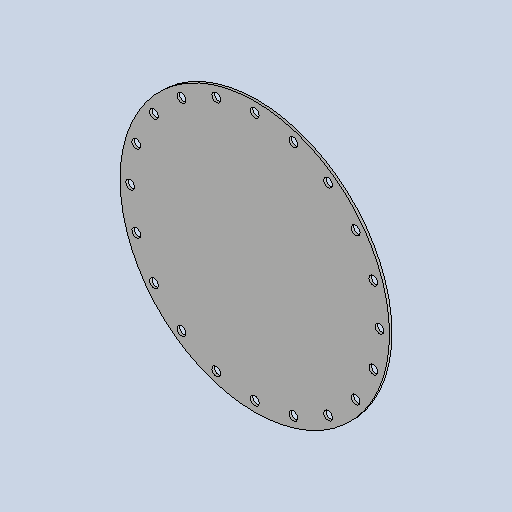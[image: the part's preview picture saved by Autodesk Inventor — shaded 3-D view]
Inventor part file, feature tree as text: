
AUTODESK INVENTOR PART (.ipt)
format: ipt  version: 2025.1 (Build 291241020, 241B)  size: 163,840 bytes
history: native  units: mm
features: sketch x2, other x2, extrude x1, pattern_circular x1
ambient origin geometry x8: Origin, YZ Plane, XZ Plane, XY Plane, X Axis, Y Axis, Z Axis, Center Point
bodies: Solid1 (feature_tree)
feature tree (6):
  extrude  "Extrusion1"  Depth=6.0mm TaperAngle=0.0deg
  pattern_circular  "Circular Pattern1"  Count=62  [1 undecoded]
  sketch  "Sketch1"  dims[d0=670.0mm d1=6.0mm d2=0.0mm]
  sketch  "Sketch2"  dims[d3=22.0mm d4=620.0mm d5=8.0mm d6=8.0mm d7=0.0mm d8=200.0mm d9=360.0deg]
  other  "Cut1"
  other  "Definition1"
note: 1 required parameter value undecoded (feature->parameter linkage not recoverable at this tier; creation-order binding heuristic only, values carry confidence <= 0.55)
